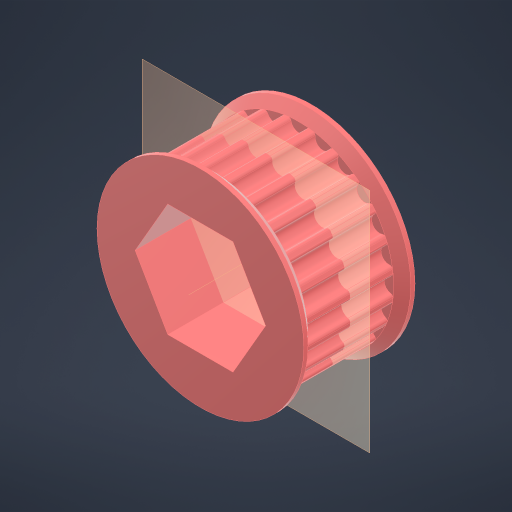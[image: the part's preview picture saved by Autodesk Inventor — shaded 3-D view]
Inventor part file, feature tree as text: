
AUTODESK INVENTOR PART (.ipt)
format: ipt  version: 2023.4 (Build 274418000, 418)  size: 408,576 bytes
history: native  units: in
note: dims shown in document units (in); Inventor stores cm internally (conversion verified against a paired STEP export)
features: extrude x6, mirror x2, chamfer x2, other x1, fillet x1, pattern_circular x1
ambient origin geometry x8: Origin, YZ Plane, XZ Plane, XY Plane, X Axis, Y Axis, Z Axis, Center Point
bodies: Solid1 (feature_tree)
feature tree (13):
  other  "Hex Bore"
  extrude  "HTD Base"  Depth=1.4588in
  extrude  "HTD Flange"  Depth=0.3937in TaperAngle=0.0deg
  mirror  "HTD Flanges"
  chamfer  "HTD Flange Chamfer"  Distance=0.0394in
  extrude  "GT2 Base"  Depth=0.0591in
  extrude  "GT2 Base Tooth"  TaperAngle=0.0deg  [1 undecoded]
  fillet  "GT2 Base Tooth pt. 2"  Radius=0.0394in
  pattern_circular  "GT2 Teeth"  Angle=45.0deg  [1 undecoded]
  extrude  "GT2 Flange"  Depth=0.52in
  mirror  "GT2 Flanges"
  chamfer  "GT2 Flange Chamfer"  [1 undecoded]
  extrude  "Circle Bore"  Depth=0.52in
note: 3 required parameter values undecoded (feature->parameter linkage not recoverable at this tier; creation-order binding heuristic only, values carry confidence <= 0.55)
